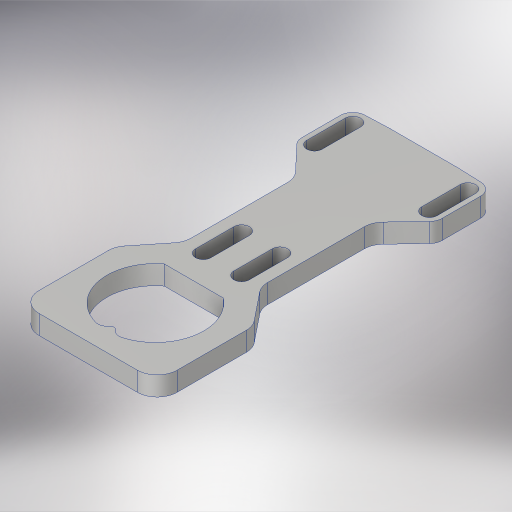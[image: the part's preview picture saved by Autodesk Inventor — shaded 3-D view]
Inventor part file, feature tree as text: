
AUTODESK INVENTOR PART (.ipt)
format: ipt  version: 2023.4 (Build 274418000, 418)  size: 726,016 bytes
history: native  units: in
note: dims shown in document units (in); Inventor stores cm internally (conversion verified against a paired STEP export)
features: extrude x8, sketch x7, fillet x7, other x7, projected_geometry x5
ambient origin geometry x8: Origin, YZ Plane, XZ Plane, XY Plane, X Axis, Y Axis, Z Axis, Center Point
bodies: Solid1 (feature_tree)
feature tree (34):
  sketch  "Sketch1"  dims[d1=0.7in d3=0.13in]
  extrude  "Extrusion1"  Depth=0.13in
  extrude  "Extrusion2"  Depth=0.197in
  extrude  "Extrusion3"  Depth=3.0in
  extrude  "Extrusion4"  Depth=0.25in
  fillet  "Fillet3"  Radius=0.25in
  extrude  "Extrusion5"  Depth=0.25in
  fillet  "Fillet4"  Radius=0.5in
  extrude  "Extrusion6"  Depth=0.5in
  extrude  "Extrusion7"  Depth=0.0625in
  fillet  "Fillet5"  Radius=0.5in
  other  "Full Round Fillet3"
  other  "Full Round Fillet4"
  other  "Full Round Fillet5"
  other  "Full Round Fillet6"
  other  "Full Round Fillet7"
  other  "Full Round Fillet8"
  other  "Full Round Fillet9"
  fillet  "Fillet6"  Radius=0.125in
  fillet  "Fillet8"  Radius=1.0in
  extrude  "Extrusion8"  Depth=0.0625in
  fillet  "Fillet7"  Radius=0.042in
  fillet  "Fillet9"  Radius=1.0in
  sketch  "Sketch2"  dims[d4=0.197in d5=0.197in]
  sketch  "Sketch3"  dims[d8=1.0in d9=3.0in]
  sketch  "Sketch4"  dims[d10=0.25in d11=0.5in d12=0.25in]
  sketch  "Sketch5"  dims[d13=0.25in d14=0.0in d23=0.201in d24=0.5in]
  sketch  "Sketch8"  dims[d26=2.3753in d27=0.5in]
  sketch  "Sketch9"  dims[d28=1.0in d29=0.0in d30=1.26in d31=0.5in d32=0.125in d33=1.0in d34=0.0in d36=0.093in d37=0.042in d38=1.0in d39=0.0in d40=0.125in d41=0.7874in d43=0.197in d44=0.3937in d46=1.0in d51=1.0in d52=0.0in d53=0.26in d54=1.5748in d56=0.197in d57=0.3937in d59=1.0in d61=1.8in d62=1.25in d64=1.75in d70=0.175in d71=0.0in d74=1.5in d75=0.06in d76=0.0in d77=0.13in d78=0.0625in d80=0.201in d81=1.5in d82=0.675in d83=0.5in d84=0.0625in d85=0.0625in d86=0.5in d87=0.06in d88=0.0in d89=0.26in d90=0.0625in d91=0.0625in]
  projected_geometry  "Project Cut Edges1"
  projected_geometry  "Project Cut Edges2"
  projected_geometry  "Project Cut Edges3"
  projected_geometry  "Project Cut Edges4"
  projected_geometry  "Project Cut Edges7"
